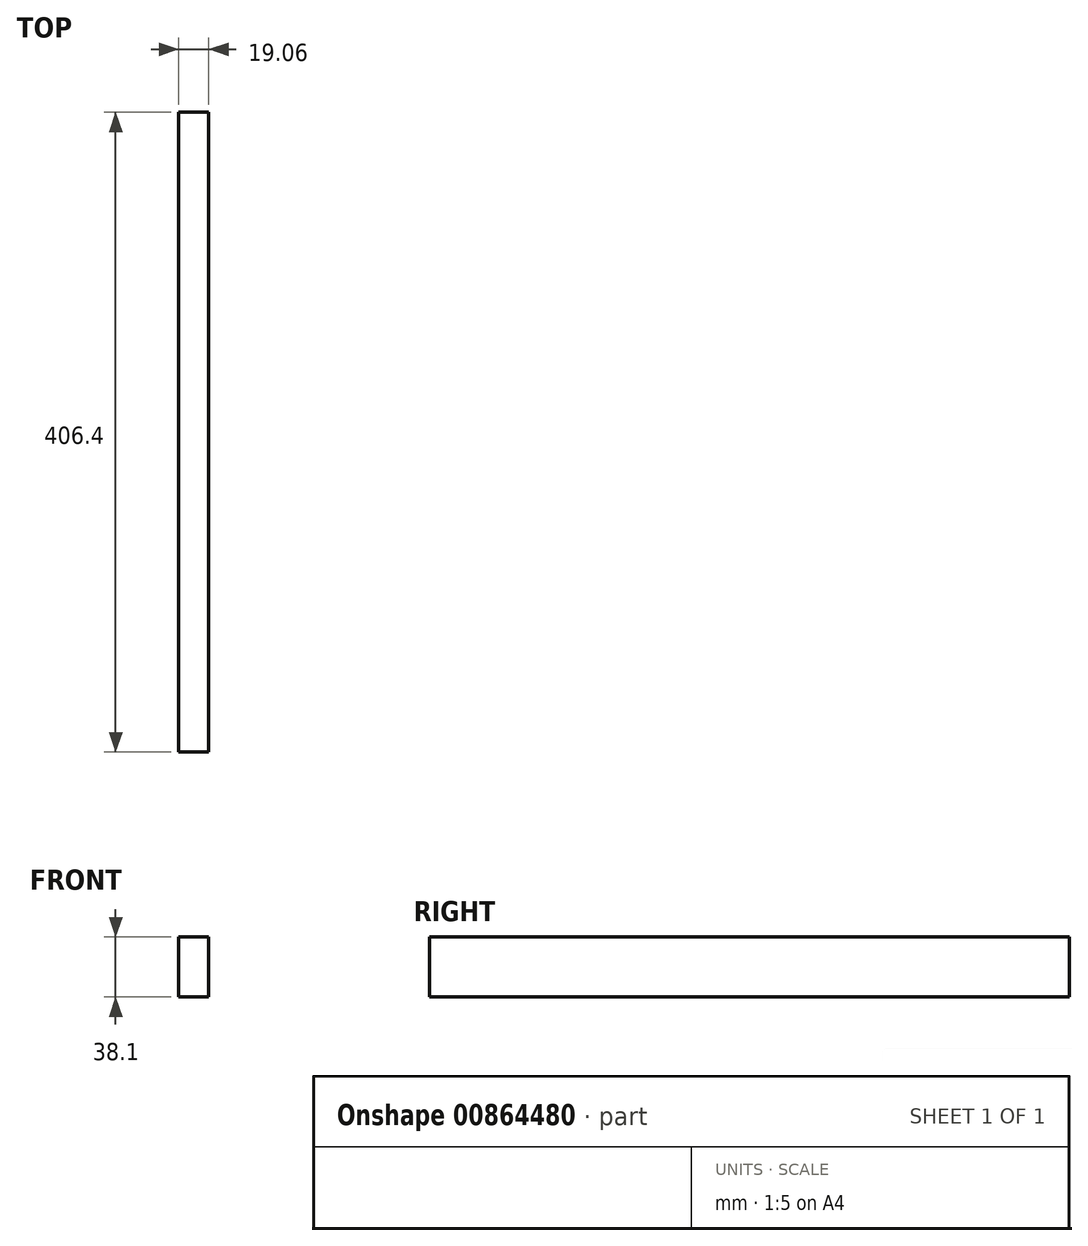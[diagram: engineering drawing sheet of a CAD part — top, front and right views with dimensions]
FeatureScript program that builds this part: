
annotation { "Feature Type Name" : "Feature", "Feature Type Description" : "" }
export const myFeature = defineFeature(function(context is Context, id is Id, definition is map)
    precondition{}
    {
        {
            var Q0;
            Q0=qCreatedBy(makeId("Front.planeOp"),FACE);
            var sketch = newSketch(context, id + "F0", { "sketchPlane" : qUnion([Q0])});
            skLineSegment(sketch, "E0.bottom", {"start": v(9.53, 19.05) * mm, "end": v(-9.53, 19.05) * mm});
            skLineSegment(sketch, "E0.top", {"start": v(9.53, -19.05) * mm, "end": v(-9.53, -19.05) * mm});
            skLineSegment(sketch, "E0.left", {"start": v(9.53, 19.05) * mm, "end": v(9.53, -19.05) * mm});
            skLineSegment(sketch, "E0.right", {"start": v(-9.52, 19.05) * mm, "end": v(-9.53, -19.05) * mm});
            skPoint(sketch, "E0.middle", {"position": v(0, 0) * mm});
            skSolve(sketch);
        }
        {
            var Q0;
            Q0=makeQuery(id+"F0.imprint","IMPRINT",FACE,{"disambiguationData":[TD([[makeQuery(id+"F0.imprint","IMPRINT",EDGE,{"derivedFrom":sQuery(id+"F0.wireOp",EDGE,"E0.bottom")}),1.0]])]});
            extrude(context, id + "F1", {"entities" : qUnion([Q0]), "depth" : 406.4 * mm, "offsetDistance" : 25.4 * mm});
        }
    });
